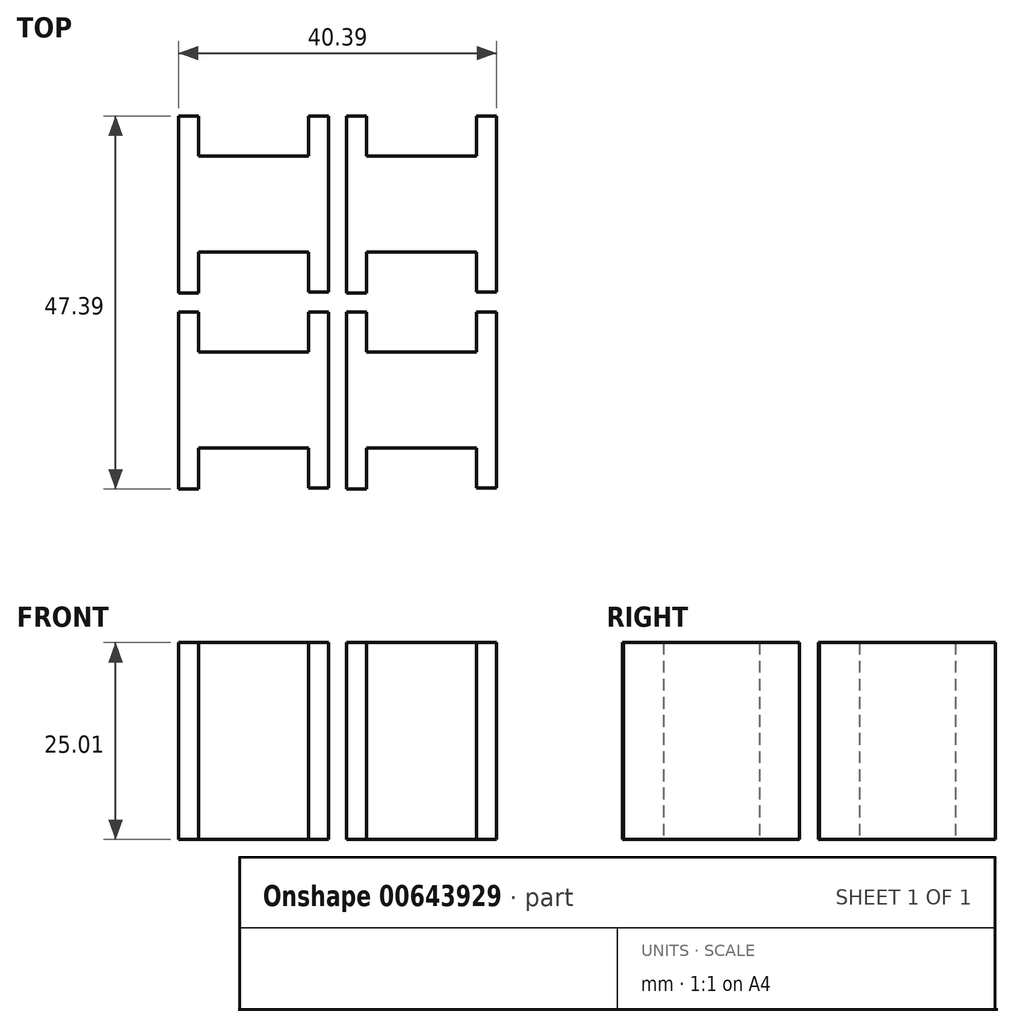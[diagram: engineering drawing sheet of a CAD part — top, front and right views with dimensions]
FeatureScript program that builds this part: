
annotation { "Feature Type Name" : "Feature", "Feature Type Description" : "" }
export const myFeature = defineFeature(function(context is Context, id is Id, definition is map)
    precondition{}
    {
        {
            var Q0;
            Q0=qCreatedBy(makeId("Top.planeOp"),FACE);
            var sketch = newSketch(context, id + "F0", { "sketchPlane" : qUnion([Q0])});
            skLineSegment(sketch, "E0.bottom", {"start": v(-6.99, 6.1) * mm, "end": v(6.99, 6.1) * mm});
            skLineSegment(sketch, "E0.top", {"start": v(-6.98, -6.1) * mm, "end": v(6.98, -6.1) * mm});
            skLineSegment(sketch, "E0.left", {"start": v(-6.99, 6.1) * mm, "end": v(-6.99, -6.1) * mm});
            skLineSegment(sketch, "E0.right", {"start": v(6.98, 6.1) * mm, "end": v(6.98, -6.1) * mm});
            skPoint(sketch, "E0.middle", {"position": v(0, 0) * mm});
            skLineSegment(sketch, "E1", {"start": v(-6.99, 6.1) * mm, "end": v(-6.99, 11.18) * mm});
            skLineSegment(sketch, "E2", {"start": v(-6.99, 11.18) * mm, "end": v(-9.53, 11.18) * mm});
            skLineSegment(sketch, "E3", {"start": v(-6.98, -6.1) * mm, "end": v(-6.98, -11.32) * mm});
            skLineSegment(sketch, "E4", {"start": v(-6.98, -11.32) * mm, "end": v(-9.52, -11.32) * mm});
            skLineSegment(sketch, "E5", {"start": v(-9.52, -11.32) * mm, "end": v(-9.53, 11.18) * mm});
            skLineSegment(sketch, "E6", {"start": v(6.99, 6.1) * mm, "end": v(6.99, 11.18) * mm});
            skLineSegment(sketch, "E7", {"start": v(6.99, 11.18) * mm, "end": v(9.53, 11.18) * mm});
            skLineSegment(sketch, "E8", {"start": v(6.98, -6.1) * mm, "end": v(6.98, -11.18) * mm});
            skLineSegment(sketch, "E9", {"start": v(6.98, -11.18) * mm, "end": v(9.52, -11.18) * mm});
            skLineSegment(sketch, "E10", {"start": v(9.52, -11.18) * mm, "end": v(9.53, 11.18) * mm});
            skSolve(sketch);
        }
        {
            var Q0;
            Q0=makeQuery(id+"F0.imprint","IMPRINT",FACE,{"disambiguationData":[TD([[makeQuery(id+"F0.imprint","IMPRINT",EDGE,{"derivedFrom":sQuery(id+"F0.wireOp",EDGE,"E0.right")}),1.0]])]});
            var Q1;
            Q1=makeQuery(id+"F0.imprint","IMPRINT",FACE,{"disambiguationData":[TD([[makeQuery(id+"F0.imprint","IMPRINT",EDGE,{"derivedFrom":sQuery(id+"F0.wireOp",EDGE,"E0.bottom")}),-1.0]])]});
            var Q2;
            Q2=makeQuery(id+"F0.imprint","IMPRINT",FACE,{"disambiguationData":[TD([[makeQuery(id+"F0.imprint","IMPRINT",EDGE,{"derivedFrom":sQuery(id+"F0.wireOp",EDGE,"E0.left")}),-1.0]])]});
            extrude(context, id + "F1", {"entities" : qUnion([Q0, Q1, Q2]), "depth" : 25 * mm, "offsetDistance" : 25.4 * mm});
        }
        {
            var Q0;
            Q0=makeQuery(id+"F1.opExtrude","SWEPT_BODY",BODY,{"disambiguationData":[OSD([sQuery(id+"F0.wireOp",EDGE,"E0.bottom"),sQuery(id+"F0.wireOp",EDGE,"E0.top"),sQuery(id+"F0.wireOp",EDGE,"E1"),sQuery(id+"F0.wireOp",EDGE,"E2"),sQuery(id+"F0.wireOp",EDGE,"E3"),sQuery(id+"F0.wireOp",EDGE,"E4"),sQuery(id+"F0.wireOp",EDGE,"E5"),sQuery(id+"F0.wireOp",EDGE,"E6"),sQuery(id+"F0.wireOp",EDGE,"E7"),sQuery(id+"F0.wireOp",EDGE,"E8"),sQuery(id+"F0.wireOp",EDGE,"E9"),sQuery(id+"F0.wireOp",EDGE,"E10")])]});
            transform(context, id + "F2", {"entities" : qUnion([Q0]), "transformType" : TransformType.TRANSLATION_3D, "dx" : 0 * mm, "dy" : 24.9 * mm, "dz" : 0 * mm, "makeCopy" : true});
        }
        {
            var Q0;
            Q0=makeQuery(id+"F1.opExtrude","SWEPT_BODY",BODY,{"disambiguationData":[OSD([sQuery(id+"F0.wireOp",EDGE,"E0.bottom"),sQuery(id+"F0.wireOp",EDGE,"E0.top"),sQuery(id+"F0.wireOp",EDGE,"E1"),sQuery(id+"F0.wireOp",EDGE,"E2"),sQuery(id+"F0.wireOp",EDGE,"E3"),sQuery(id+"F0.wireOp",EDGE,"E4"),sQuery(id+"F0.wireOp",EDGE,"E5"),sQuery(id+"F0.wireOp",EDGE,"E6"),sQuery(id+"F0.wireOp",EDGE,"E7"),sQuery(id+"F0.wireOp",EDGE,"E8"),sQuery(id+"F0.wireOp",EDGE,"E9"),sQuery(id+"F0.wireOp",EDGE,"E10")])]});
            transform(context, id + "F3", {"entities" : qUnion([Q0]), "transformType" : TransformType.TRANSLATION_3D, "dx" : 39.12 * mm, "dy" : 0 * mm, "dz" : 0 * mm, "makeCopy" : true});
        }
        {
            var Q0;
            Q0=makeQuery(id+"F2.opPattern","COPY",BODY,{"derivedFrom":makeQuery(id+"F1.opExtrude","SWEPT_BODY",BODY,{"disambiguationData":[OSD([sQuery(id+"F0.wireOp",EDGE,"E0.bottom"),sQuery(id+"F0.wireOp",EDGE,"E0.top"),sQuery(id+"F0.wireOp",EDGE,"E1"),sQuery(id+"F0.wireOp",EDGE,"E2"),sQuery(id+"F0.wireOp",EDGE,"E3"),sQuery(id+"F0.wireOp",EDGE,"E4"),sQuery(id+"F0.wireOp",EDGE,"E5"),sQuery(id+"F0.wireOp",EDGE,"E6"),sQuery(id+"F0.wireOp",EDGE,"E7"),sQuery(id+"F0.wireOp",EDGE,"E8"),sQuery(id+"F0.wireOp",EDGE,"E9"),sQuery(id+"F0.wireOp",EDGE,"E10")])]}),"instanceName":"1"});
            transform(context, id + "F4", {"entities" : qUnion([Q0]), "transformType" : TransformType.TRANSLATION_3D, "dx" : 39.12 * mm, "dy" : -0.25 * mm, "dz" : 0 * mm, "makeCopy" : true});
        }
        {
            var Q0;
            Q0=makeQuery(id+"F3.opPattern","COPY",BODY,{"derivedFrom":makeQuery(id+"F1.opExtrude","SWEPT_BODY",BODY,{"disambiguationData":[OSD([sQuery(id+"F0.wireOp",EDGE,"E0.bottom"),sQuery(id+"F0.wireOp",EDGE,"E0.top"),sQuery(id+"F0.wireOp",EDGE,"E1"),sQuery(id+"F0.wireOp",EDGE,"E2"),sQuery(id+"F0.wireOp",EDGE,"E3"),sQuery(id+"F0.wireOp",EDGE,"E4"),sQuery(id+"F0.wireOp",EDGE,"E5"),sQuery(id+"F0.wireOp",EDGE,"E6"),sQuery(id+"F0.wireOp",EDGE,"E7"),sQuery(id+"F0.wireOp",EDGE,"E8"),sQuery(id+"F0.wireOp",EDGE,"E9"),sQuery(id+"F0.wireOp",EDGE,"E10")])]}),"instanceName":"1"});
            var Q1;
            Q1=makeQuery(id+"F4.opPattern","COPY",BODY,{"derivedFrom":makeQuery(id+"F2.opPattern","COPY",BODY,{"derivedFrom":makeQuery(id+"F1.opExtrude","SWEPT_BODY",BODY,{"disambiguationData":[OSD([sQuery(id+"F0.wireOp",EDGE,"E0.bottom"),sQuery(id+"F0.wireOp",EDGE,"E0.top"),sQuery(id+"F0.wireOp",EDGE,"E1"),sQuery(id+"F0.wireOp",EDGE,"E2"),sQuery(id+"F0.wireOp",EDGE,"E3"),sQuery(id+"F0.wireOp",EDGE,"E4"),sQuery(id+"F0.wireOp",EDGE,"E5"),sQuery(id+"F0.wireOp",EDGE,"E6"),sQuery(id+"F0.wireOp",EDGE,"E7"),sQuery(id+"F0.wireOp",EDGE,"E8"),sQuery(id+"F0.wireOp",EDGE,"E9"),sQuery(id+"F0.wireOp",EDGE,"E10")])]}),"instanceName":"1"}),"instanceName":"1"});
            deleteBodies(context, id + "F5", {"entities" : qUnion([Q0, Q1])});
        }
        {
            var Q0;
            Q0=makeQuery(id+"F1.opExtrude","SWEPT_BODY",BODY,{"disambiguationData":[OSD([sQuery(id+"F0.wireOp",EDGE,"E0.bottom"),sQuery(id+"F0.wireOp",EDGE,"E0.top"),sQuery(id+"F0.wireOp",EDGE,"E1"),sQuery(id+"F0.wireOp",EDGE,"E2"),sQuery(id+"F0.wireOp",EDGE,"E3"),sQuery(id+"F0.wireOp",EDGE,"E4"),sQuery(id+"F0.wireOp",EDGE,"E5"),sQuery(id+"F0.wireOp",EDGE,"E6"),sQuery(id+"F0.wireOp",EDGE,"E7"),sQuery(id+"F0.wireOp",EDGE,"E8"),sQuery(id+"F0.wireOp",EDGE,"E9"),sQuery(id+"F0.wireOp",EDGE,"E10")])]});
            transform(context, id + "F6", {"entities" : qUnion([Q0]), "transformType" : TransformType.TRANSLATION_3D, "dx" : 21.34 * mm, "dy" : 0 * mm, "dz" : 0 * mm, "makeCopy" : true});
        }
        {
            var Q0;
            Q0=makeQuery(id+"F2.opPattern","COPY",BODY,{"derivedFrom":makeQuery(id+"F1.opExtrude","SWEPT_BODY",BODY,{"disambiguationData":[OSD([sQuery(id+"F0.wireOp",EDGE,"E0.bottom"),sQuery(id+"F0.wireOp",EDGE,"E0.top"),sQuery(id+"F0.wireOp",EDGE,"E1"),sQuery(id+"F0.wireOp",EDGE,"E2"),sQuery(id+"F0.wireOp",EDGE,"E3"),sQuery(id+"F0.wireOp",EDGE,"E4"),sQuery(id+"F0.wireOp",EDGE,"E5"),sQuery(id+"F0.wireOp",EDGE,"E6"),sQuery(id+"F0.wireOp",EDGE,"E7"),sQuery(id+"F0.wireOp",EDGE,"E8"),sQuery(id+"F0.wireOp",EDGE,"E9"),sQuery(id+"F0.wireOp",EDGE,"E10")])]}),"instanceName":"1"});
            transform(context, id + "F7", {"entities" : qUnion([Q0]), "transformType" : TransformType.TRANSLATION_3D, "dx" : 21.34 * mm, "dy" : 0 * mm, "dz" : 0 * mm, "makeCopy" : true});
        }
    });
